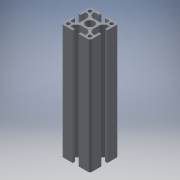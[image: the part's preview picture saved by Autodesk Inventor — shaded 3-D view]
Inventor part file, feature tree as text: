
AUTODESK INVENTOR PART (.ipt)
format: ipt  version: 2018 (Build 220112000, 112)  size: 200,704 bytes
history: native  units: mm
features: other x42, sketch x5, hole x4, extrude x1
ambient origin geometry x8: Origin, YZ Plane, XZ Plane, XY Plane, X Axis, Y Axis, Z Axis, Center Point
bodies: Solid1 (feature_tree)
feature tree (52):
  extrude  "Extrusion1"  [1 undecoded]
  hole  "Drilling 1"  [1 undecoded]
  hole  "Drilling 2"  [1 undecoded]
  hole  "Drilling 3"  [1 undecoded]
  hole  "Drilling 4"  [1 undecoded]
  other  "side_4d_XY"
  other  "side_4d_YZ"
  other  "side_4d_ZX"
  other  "side_4d_X"
  other  "side_4d_Y"
  other  "side_4d_Z"
  other  "side_4d_Center"
  other  "side_1a_XY"
  other  "side_1a_YZ"
  other  "side_1a_ZX"
  other  "side_1a_X"
  other  "side_1a_Y"
  other  "side_1a_Z"
  other  "side_1a_Center"
  other  "side_2b_XY"
  other  "side_2b_YZ"
  other  "side_2b_ZX"
  other  "side_2b_X"
  other  "side_2b_Y"
  other  "side_2b_Z"
  other  "side_2b_Center"
  other  "side_3c_XY"
  other  "side_3c_YZ"
  other  "side_3c_ZX"
  other  "side_3c_X"
  other  "side_3c_Y"
  other  "side_3c_Z"
  other  "side_3c_Center"
  other  "end_XY"
  other  "end_YZ"
  other  "end_ZX"
  other  "end_X"
  other  "end_Y"
  other  "end_Z"
  other  "end_Center"
  other  "start_XY"
  other  "start_YZ"
  other  "start_ZX"
  other  "start_X"
  other  "start_Y"
  other  "start_Z"
  other  "start_Center"
  sketch  "Skizze_1"  dims[d0=160.0mm d1=0.0mm]
  sketch  "Sketch2"  dims[d2=5.0mm d3=6.0mm d4=4.0mm d5=2.0mm d6=90.0deg d7=6000.0mm d8=0.0mm]
  sketch  "Sketch3"  dims[d9=5.0mm d10=6.0mm d11=4.0mm d12=2.0mm d13=90.0deg d14=6000.0mm d15=0.0mm]
  sketch  "Sketch4"  dims[d16=5.0mm d17=6.0mm d18=4.0mm d19=2.0mm d20=90.0deg d21=6000.0mm d22=0.0mm]
  sketch  "Sketch5"  dims[d23=5.0mm d24=6.0mm d25=4.0mm d26=2.0mm d27=90.0deg d28=6000.0mm d29=0.0mm]
note: 5 required parameter values undecoded (feature->parameter linkage not recoverable at this tier; creation-order binding heuristic only, values carry confidence <= 0.55)
